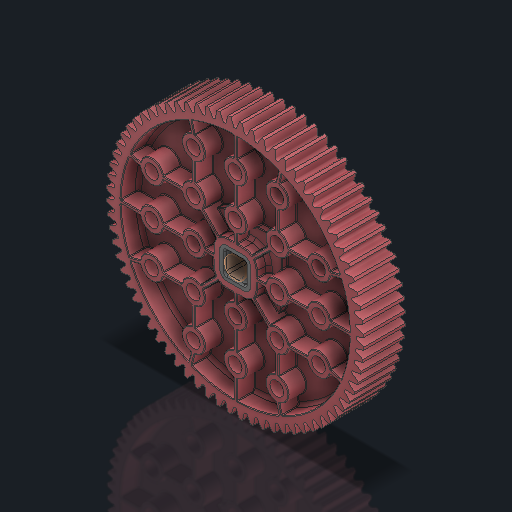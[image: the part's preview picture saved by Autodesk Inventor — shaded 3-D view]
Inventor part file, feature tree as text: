
AUTODESK INVENTOR PART (.ipt)
format: ipt  version: 2023.2 (Build 272271030, 271C)  size: 6,659,584 bytes
history: native  units: in
note: dims shown in document units (in); Inventor stores cm internally (conversion verified against a paired STEP export)
features: other x6, sketch x1
ambient origin geometry x8: Origin, YZ Plane, XZ Plane, XY Plane, X Axis, Y Axis, Z Axis, Center Point
bodies: Solid1 (feature_tree), Solid2 (feature_tree)
feature tree (7):
  other  "HS 72T Gear, No Insert.ipt"
  other  "Solid1::HS 72T Gear, No Insert.ipt"
  other  "Solid2::HS 72T Gear, No Insert.ipt"
  other  "TaggingFeature1"
  sketch  "Sketch1"  dims[d0=0.3937in]
  other  "Srf1"
  other  "Srf1::Derived"
